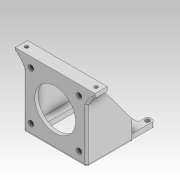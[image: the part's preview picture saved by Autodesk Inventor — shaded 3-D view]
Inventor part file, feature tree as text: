
AUTODESK INVENTOR PART (.ipt)
format: ipt  version: 2020 (Build 240168000, 168)  size: 327,168 bytes
history: native  units: mm
features: extrude x10, sketch x10, fillet x4, mirror x2, plane x1, chamfer x1, projected_geometry x1
ambient origin geometry x8: Origin, YZ Plane, XZ Plane, XY Plane, X Axis, Y Axis, Z Axis, Center Point
bodies: Solid1 (feature_tree)
feature tree (29):
  extrude  "Extrusion1"  Depth=47.0mm
  extrude  "Extrusion2"  Depth=40.0mm
  extrude  "Extrusion3"  Depth=3.5mm TaperAngle=0.0deg
  extrude  "Extrusion4"  Depth=10.0mm
  mirror  "Mirror1"
  fillet  "Fillet1"  Radius=4.0mm
  extrude  "Extrusion5"  TaperAngle=0.0deg  [1 undecoded]
  plane  "Work Plane1"
  extrude  "Extrusion6"  Depth=25.0mm
  extrude  "Extrusion7"  Depth=5.0mm
  extrude  "Extrusion8"  TaperAngle=0.0deg  [1 undecoded]
  extrude  "Extrusion9"  Depth=10.0mm TaperAngle=0.0deg
  chamfer  "Chamfer2"  Distance=7.0mm
  mirror  "Mirror2"
  fillet  "Fillet2"  Radius=7.0mm
  fillet  "Fillet3"  Radius=9.2mm
  fillet  "Fillet4"  Radius=7.0mm
  extrude  "Extrusion10"  Depth=10.0mm TaperAngle=0.0deg
  sketch  "Sketch1"  dims[d0=5.2mm d1=47.0mm]
  sketch  "Sketch2"  dims[d2=47.0mm d3=40.0mm]
  projected_geometry  "Projected Loop1"
  sketch  "Sketch3"  dims[d4=58.0mm d5=3.5mm d6=0.0mm]
  sketch  "Sketch4"  dims[d7=10.0mm d8=12.0mm d9=4.0mm d10=0.0mm]
  sketch  "Sketch5"  dims[d15=4.0mm d16=0.0mm d18=0.0mm d19=0.0mm]
  sketch  "Sketch6"  dims[d20=45.0deg d21=25.0mm]
  sketch  "Sketch7"  dims[d22=5.0mm d23=5.0mm]
  sketch  "Sketch8"  dims[d24=3.3mm d25=0.0mm d26=0.0mm]
  sketch  "Sketch9"  dims[d27=6.0mm d28=10.0mm d29=0.0mm]
  sketch  "Sketch10"  dims[d30=-6.5mm d32=7.0mm d33=7.0mm d35=9.2mm d36=7.0mm d37=5.0mm d38=0.0mm d39=59.0mm d40=5.0mm d41=7.0mm d42=3.5mm d43=4.3mm d44=5.0mm d45=0.0mm d46=2.0mm d47=2.0mm d50=2.0mm d51=0.0mm d52=1.0mm d53=2.0mm d54=45.0deg d55=2.0mm d56=55.0mm d57=8.0mm d58=10.0mm d59=0.0mm]
note: 2 required parameter values undecoded (feature->parameter linkage not recoverable at this tier; creation-order binding heuristic only, values carry confidence <= 0.55)
